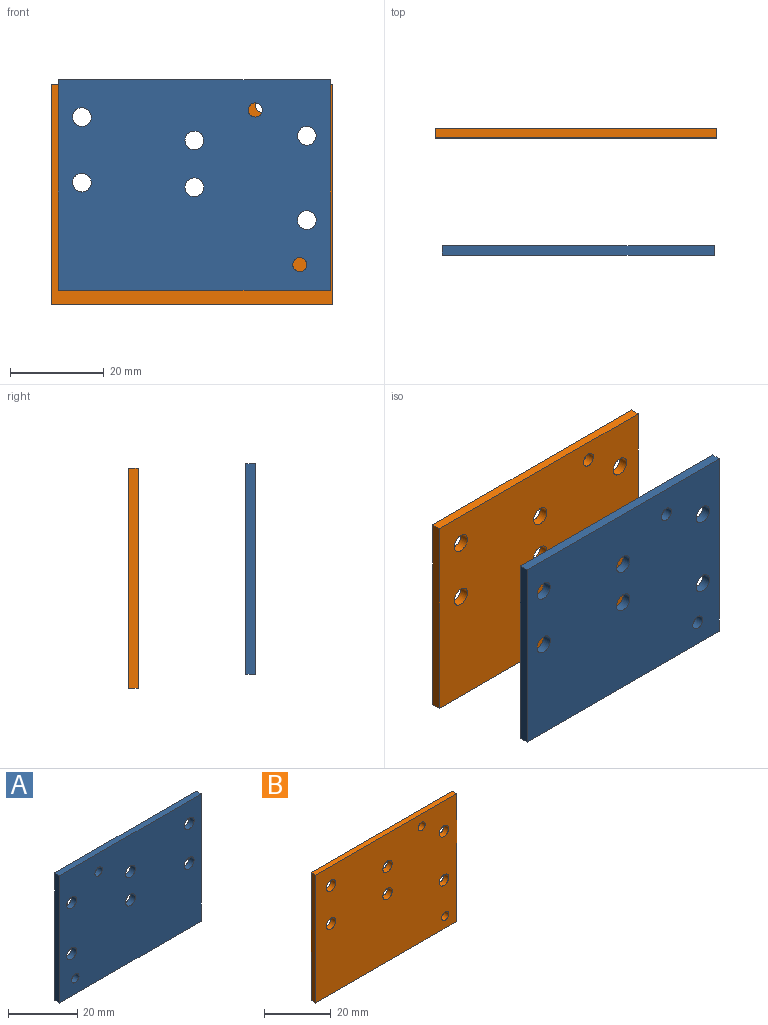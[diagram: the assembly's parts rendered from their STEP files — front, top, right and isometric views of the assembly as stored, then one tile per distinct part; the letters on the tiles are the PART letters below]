
ASSEMBLY  parts=2 mates=1
PART A: 14 faces, bbox 58x2x45 mm
  f0: plane 58x2mm, normal (0,0,1), area 116mm2, adj f1,f11,f12,f13
  f1: plane 45x2mm, normal (-1,0,0), area 90mm2, adj f0,f2,f12,f13
  f2: plane 58x2mm, normal (0,0,-1), area 116mm2, adj f1,f11,f12,f13
  f3: cylinder r=1.5mm len=3mm, axis (0,1,0), area 18.8mm2, adj f12,f13
  f4: cylinder r=1.5mm len=3mm, axis (0,1,0), area 18.8mm2, adj f12,f13
  f5: cylinder r=2mm len=4mm, axis (0,1,0), area 25.1mm2, adj f12,f13
  f6: cylinder r=2mm len=4mm, axis (0,1,0), area 25.1mm2, adj f12,f13
  f7: cylinder r=2mm len=4mm, axis (0,1,0), area 25.1mm2, adj f12,f13
  f8: cylinder r=2mm len=4mm, axis (0,1,0), area 25.1mm2, adj f12,f13
  f9: cylinder r=2mm len=4mm, axis (0,1,0), area 25.1mm2, adj f12,f13
  f10: cylinder r=2mm len=4mm, axis (0,1,0), area 25.1mm2, adj f12,f13
  f11: plane 45x2mm, normal (1,0,0), area 90mm2, adj f0,f2,f12,f13
  f12: plane 58x45mm, normal (0,-1,0), area 2520.5mm2, adj f0,f1,f2,f3,f4,f5,f6,f7
  f13: plane 58x45mm, normal (0,1,0), area 2520.5mm2, adj f0,f1,f2,f3,f4,f5,f6,f7
PART B: 14 faces, bbox 60x2x47 mm
  f0: plane 60x2mm, normal (0,0,1), area 120mm2, adj f1,f11,f12,f13
  f1: plane 47x2mm, normal (-1,0,0), area 94mm2, adj f0,f2,f12,f13
  f2: plane 60x2mm, normal (0,0,-1), area 120mm2, adj f1,f11,f12,f13
  f3: cylinder r=1.5mm len=3mm, axis (0,1,0), area 18.8mm2, adj f12,f13
  f4: cylinder r=1.5mm len=3mm, axis (0,1,0), area 18.8mm2, adj f12,f13
  f5: cylinder r=2mm len=4mm, axis (0,1,0), area 25.1mm2, adj f12,f13
  f6: cylinder r=2mm len=4mm, axis (0,1,0), area 25.1mm2, adj f12,f13
  f7: cylinder r=2mm len=4mm, axis (0,1,0), area 25.1mm2, adj f12,f13
  f8: cylinder r=2mm len=4mm, axis (0,1,0), area 25.1mm2, adj f12,f13
  f9: cylinder r=2mm len=4mm, axis (0,1,0), area 25.1mm2, adj f12,f13
  f10: cylinder r=2mm len=4mm, axis (0,1,0), area 25.1mm2, adj f12,f13
  f11: plane 47x2mm, normal (1,0,0), area 94mm2, adj f0,f2,f12,f13
  f12: plane 60x47mm, normal (0,-1,0), area 2730.5mm2, adj f0,f1,f2,f3,f4,f5,f6,f7
  f13: plane 60x47mm, normal (0,1,0), area 2730.5mm2, adj f0,f1,f2,f3,f4,f5,f6,f7
PLACE A rot(axis=(0,0,-1),180deg) t=(11.6,3.74,0)mm
PLACE B t=(-0.3,30.74,7.97)mm
MATE cylindrical B.f6 <-> A.f6  axis (0,1,0) through (25.61,30.74,-5.76)mm
